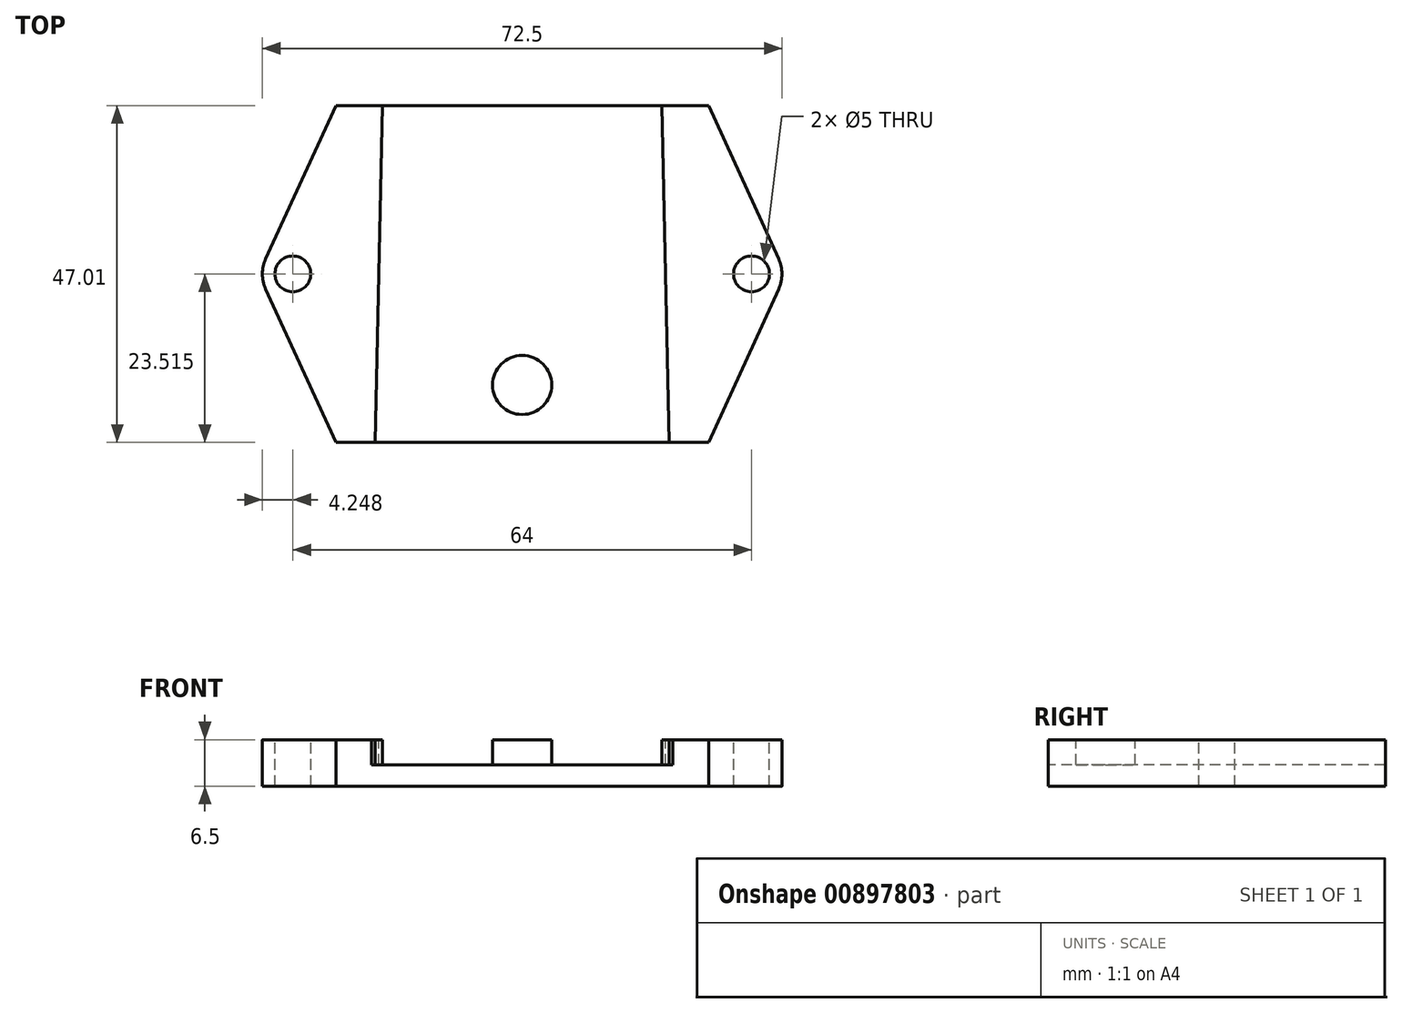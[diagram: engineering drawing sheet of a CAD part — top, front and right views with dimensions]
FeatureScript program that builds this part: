
annotation { "Feature Type Name" : "Feature", "Feature Type Description" : "" }
export const myFeature = defineFeature(function(context is Context, id is Id, definition is map)
    precondition{}
    {
        {
            var Q0;
            Q0=qCreatedBy(makeId("Top.planeOp"),FACE);
            var sketch = newSketch(context, id + "F0", { "sketchPlane" : qUnion([Q0])});
            skLineSegment(sketch, "E0.bottom", {"start": v(-22.7, 19.47) * mm, "end": v(29.3, 19.47) * mm});
            skLineSegment(sketch, "E0.top", {"start": v(-22.7, -27.53) * mm, "end": v(29.3, -27.53) * mm});
            skLineSegment(sketch, "E1", {"start": v(-22.7, 19.47) * mm, "end": v(-33.45, -4.03) * mm});
            skLineSegment(sketch, "E2", {"start": v(-33.45, -4.03) * mm, "end": v(-22.7, -27.53) * mm});
            skLineSegment(sketch, "E3", {"start": v(29.3, 19.47) * mm, "end": v(40.05, -4.03) * mm});
            skLineSegment(sketch, "E4", {"start": v(40.05, -4.03) * mm, "end": v(29.3, -27.53) * mm});
            skCircle(sketch, "E5", {"center": v(35.3, -4.03) * mm, "radius": 2.5 * mm});
            skCircle(sketch, "E6", {"center": v(-28.7, -4.03) * mm, "radius": 2.5 * mm});
            skLineSegment(sketch, "E7", {"start": v(-16.7, 19.47) * mm, "end": v(-17.7, -27.53) * mm});
            skLineSegment(sketch, "E8", {"start": v(23.3, 19.47) * mm, "end": v(24.3, -27.53) * mm});
            skCircle(sketch, "E9", {"center": v(3.3, -19.53) * mm, "radius": 4.12 * mm});
            skSolve(sketch);
        }
        {
            var Q0;
            Q0 = qSketchRegion(id + "F0", true);
            var Q1;
            Q1=makeQuery(id+"F0.imprint","IMPRINT",FACE,{"disambiguationData":[TD([[makeQuery(id+"F0.imprint","IMPRINT",EDGE,{"derivedFrom":sQuery(id+"F0.wireOp",EDGE,"AzOQRoRA-1GN4-h1HK-NjRR-aouzdl7ZBtMV")}),1.0]])]});
            var Q2;
            Q2=makeQuery(id+"F0.imprint","IMPRINT",FACE,{"disambiguationData":[TD([[makeQuery(id+"F0.imprint","IMPRINT",EDGE,{"derivedFrom":sQuery(id+"F0.wireOp",EDGE,"E9")}),1.0]])]});
            extrude(context, id + "F1", {"entities" : qUnion([Q0, Q1, Q2]), "oppositeDirection" : true, "depth" : 6.5 * mm, "offsetDistance" : 25 * mm});
        }
        {
            var Q0;
            {var subQ1=sQuery(id+"F0.wireOp",EDGE,"E7");Q0=makeQuery(id+"F0.imprint","IMPRINT",FACE,{"disambiguationData":[TD([[makeQuery(id+"F0.imprint","IMPRINT",EDGE,{"derivedFrom":subQ1}),1.0]])]});}
            extrude(context, id + "F2", {"entities" : qUnion([Q0]), "operationType" : NewBodyOperationType.REMOVE, "oppositeDirection" : true, "depth" : 3.5 * mm, "offsetDistance" : 25 * mm});
        }
        {
            var Q0;
            Q0=makeQuery(id+"F1.opExtrude","SWEPT_EDGE",EDGE,{"disambiguationData":[OSD([sQuery(id+"F0.wireOp",EDGE,"E1"),sQuery(id+"F0.wireOp",EDGE,"E2")])]});
            var Q1;
            Q1=makeQuery(id+"F1.opExtrude","SWEPT_EDGE",EDGE,{"disambiguationData":[OSD([sQuery(id+"F0.wireOp",EDGE,"E3"),sQuery(id+"F0.wireOp",EDGE,"E4")])]});
            fillet(context, id + "F3", {"entities" : qUnion([Q0, Q1]), "radius" : 5 * mm, "tangentPropagation" : true, "allowEdgeOverflow" : false});
        }
        {
            var Q0;
            Q0=makeQuery(id+"F2.boolean.opBoolean","COPY",FACE,{"derivedFrom":makeQuery(id+"F2.opExtrude","SWEPT_FACE",FACE,{"disambiguationData":[OSD([sQuery(id+"F0.wireOp",EDGE,"E7")])]})});
            extrude(context, id + "F4", {"entities" : qUnion([Q0]), "operationType" : NewBodyOperationType.ADD, "surfaceOperationType" : NewSurfaceOperationType.ADD, "depth" : 0.5 * mm, "offsetDistance" : 25 * mm});
        }
        {
            var Q0;
            Q0=makeQuery(id+"F2.boolean.opBoolean","COPY",FACE,{"derivedFrom":makeQuery(id+"F2.opExtrude","SWEPT_FACE",FACE,{"disambiguationData":[OSD([sQuery(id+"F0.wireOp",EDGE,"E8")])]})});
            extrude(context, id + "F5", {"entities" : qUnion([Q0]), "operationType" : NewBodyOperationType.ADD, "depth" : 0.5 * mm, "offsetDistance" : 25 * mm});
        }
    });
